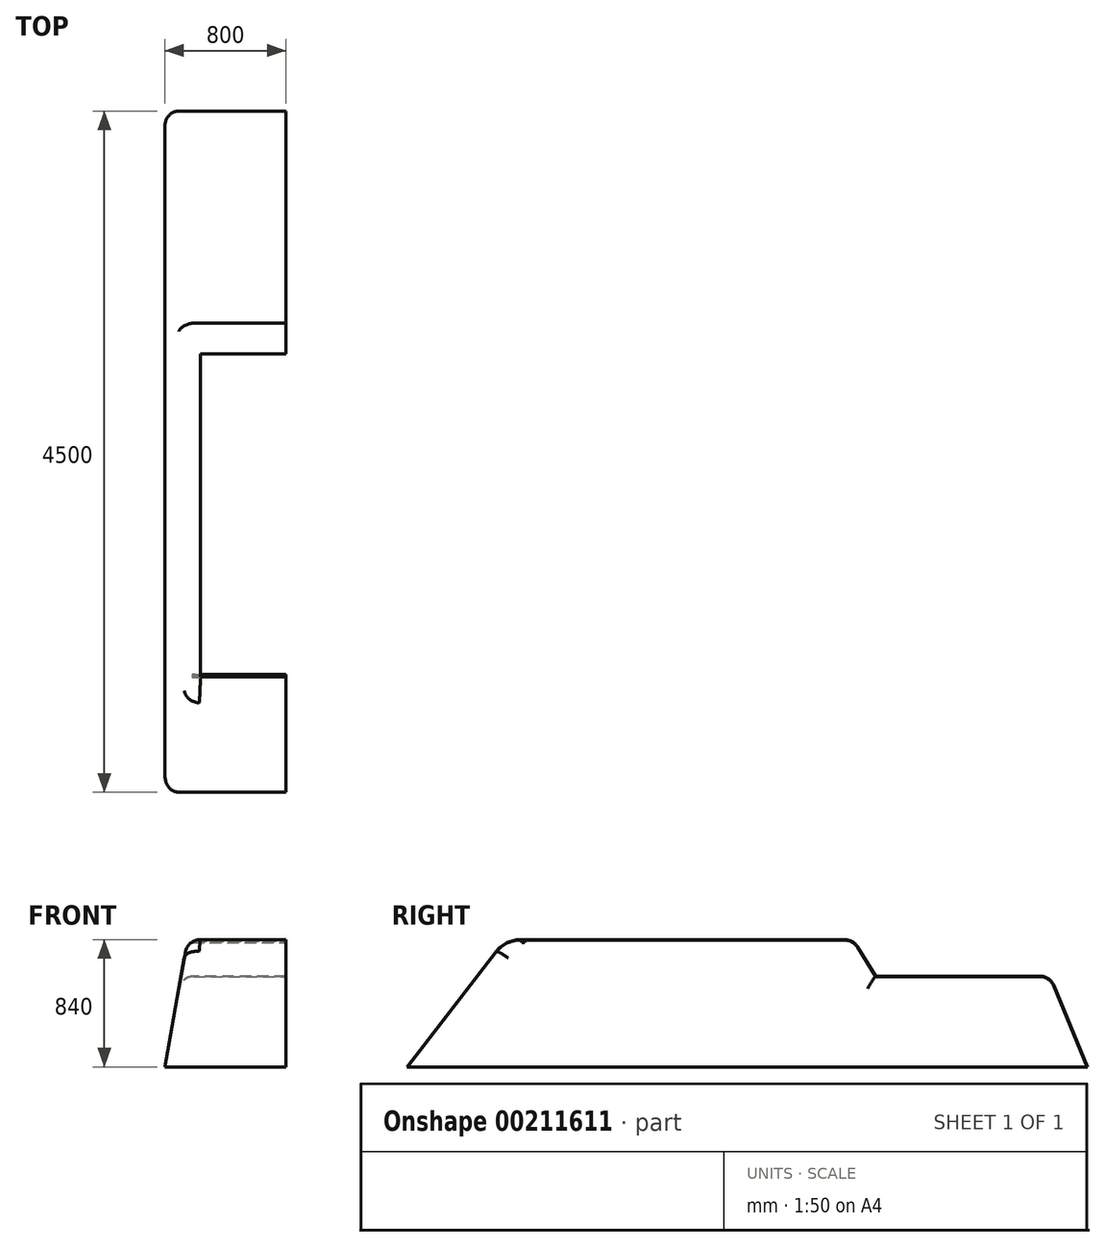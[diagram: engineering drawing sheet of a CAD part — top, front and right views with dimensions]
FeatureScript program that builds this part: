
annotation { "Feature Type Name" : "Feature", "Feature Type Description" : "" }
export const myFeature = defineFeature(function(context is Context, id is Id, definition is map)
    precondition{}
    {
        {
            var Q0;
            Q0=qCreatedBy(makeId("Right.planeOp"),FACE);
            var sketch = newSketch(context, id + "F0", { "sketchPlane" : qUnion([Q0])});
            skLineSegment(sketch, "E0", {"start": v(-1464.52, 0) * mm, "end": v(-874.57, 762.4) * mm});
            skLineSegment(sketch, "E1", {"start": v(-716.4, 840) * mm, "end": v(1430.05, 840) * mm});
            skLineSegment(sketch, "E2", {"start": v(1514.85, 793) * mm, "end": v(1635.48, 600) * mm});
            skLineSegment(sketch, "E3", {"start": v(1635.48, 600) * mm, "end": v(2718.81, 600) * mm});
            skLineSegment(sketch, "E4", {"start": v(2811.12, 538.46) * mm, "end": v(3035.48, 0) * mm});
            skLineSegment(sketch, "E5", {"start": v(3035.48, 0) * mm, "end": v(-1464.52, 0) * mm});
            skPoint(sketch, "E6.visualSharp", {"position": v(-814.52, 840) * mm});
            skArc(sketch, "E6.filletArc", {"start": v(-716.4, 840) * mm, "mid": v(-804.5, 819.55) * mm, "end": v(-874.57, 762.4) * mm});
            skPoint(sketch, "E7.visualSharp", {"position": v(1485.48, 840) * mm});
            skArc(sketch, "E7.filletArc", {"start": v(1514.85, 793) * mm, "mid": v(1478.53, 827.46) * mm, "end": v(1430.05, 840) * mm});
            skPoint(sketch, "E8.visualSharp", {"position": v(2785.48, 600) * mm});
            skArc(sketch, "E8.filletArc", {"start": v(2811.12, 538.46) * mm, "mid": v(2774.28, 583.2) * mm, "end": v(2718.81, 600) * mm});
            skSolve(sketch);
        }
        {
            var Q0;
            Q0=makeQuery(id+"F0.imprint","IMPRINT",FACE,{"disambiguationData":[TD([[makeQuery(id+"F0.imprint","IMPRINT",EDGE,{"derivedFrom":sQuery(id+"F0.wireOp",EDGE,"E0")}),-1.0]])]});
            var Q1;
            Q1=qSketchRegion(id+"FQhckZ4ycMq1syb_1",true);
            extrude(context, id + "F1", {"entities" : qUnion([Q0, Q1]), "depth" : 800 * mm});
        }
        {
            var Q0;
            Q0=qCreatedBy(makeId("Front.planeOp"),FACE);
            var sketch = newSketch(context, id + "F2", { "sketchPlane" : qUnion([Q0])});
            skLineSegment(sketch, "E9", {"start": v(0, 0) * mm, "end": v(0, 840) * mm});
            skLineSegment(sketch, "E10", {"start": v(0, 840) * mm, "end": v(150, 840) * mm});
            skLineSegment(sketch, "E11", {"start": v(150, 840) * mm, "end": v(0, 0) * mm});
            skSolve(sketch);
        }
        {
            var Q0;
            Q0=qSketchRegion(id+"F2",true);
            extrude(context, id + "F3", {"entities" : qUnion([Q0]), "operationType" : NewBodyOperationType.REMOVE, "oppositeDirection" : true, "depth" : 3490 * mm, "hasSecondDirection" : true, "secondDirectionOppositeDirection" : false, "secondDirectionDepth" : 1678 * mm});
        }
        {
            var Q0;
            Q0=makeQuery(id+"F3.boolean.opBoolean","INTERSECT",EDGE,{"derivedFrom":[makeQuery(id+"F1.opExtrude","SWEPT_FACE",FACE,{"disambiguationData":[OSD([sQuery(id+"F0.wireOp",EDGE,"E0")])]}),makeQuery(id+"F3.opExtrude","SWEPT_FACE",FACE,{"disambiguationData":[OSD([sQuery(id+"F2.wireOp",EDGE,"E11")])]})]});
            var Q1;
            Q1=makeQuery(id+"F3.boolean.opBoolean","COPY",EDGE,{"derivedFrom":makeQuery(id+"F3.opExtrude","SWEPT_EDGE",EDGE,{"disambiguationData":[OSD([sQuery(id+"F2.wireOp",EDGE,"E10"),sQuery(id+"F2.wireOp",EDGE,"E11")])]})});
            var Q2;
            Q2=makeQuery(id+"F3.boolean.opBoolean","INTERSECT",EDGE,{"derivedFrom":[makeQuery(id+"F1.opExtrude","SWEPT_FACE",FACE,{"disambiguationData":[OSD([sQuery(id+"F0.wireOp",EDGE,"E6.filletArc")])]}),makeQuery(id+"F3.opExtrude","SWEPT_FACE",FACE,{"disambiguationData":[OSD([sQuery(id+"F2.wireOp",EDGE,"E11")])]})]});
            var Q3;
            Q3=makeQuery(id+"F3.boolean.opBoolean","INTERSECT",EDGE,{"derivedFrom":[makeQuery(id+"F1.opExtrude","SWEPT_FACE",FACE,{"disambiguationData":[OSD([sQuery(id+"F0.wireOp",EDGE,"E2")])]}),makeQuery(id+"F3.opExtrude","SWEPT_FACE",FACE,{"disambiguationData":[OSD([sQuery(id+"F2.wireOp",EDGE,"E11")])]})]});
            var Q4;
            Q4=makeQuery(id+"F3.boolean.opBoolean","INTERSECT",EDGE,{"derivedFrom":[makeQuery(id+"F1.opExtrude","SWEPT_FACE",FACE,{"disambiguationData":[OSD([sQuery(id+"F0.wireOp",EDGE,"E7.filletArc")])]}),makeQuery(id+"F3.opExtrude","SWEPT_FACE",FACE,{"disambiguationData":[OSD([sQuery(id+"F2.wireOp",EDGE,"E11")])]})]});
            var Q5;
            Q5=makeQuery(id+"F3.boolean.opBoolean","INTERSECT",EDGE,{"derivedFrom":[makeQuery(id+"F1.opExtrude","SWEPT_FACE",FACE,{"disambiguationData":[OSD([sQuery(id+"F0.wireOp",EDGE,"E3")])]}),makeQuery(id+"F3.opExtrude","SWEPT_FACE",FACE,{"disambiguationData":[OSD([sQuery(id+"F2.wireOp",EDGE,"E11")])]})]});
            var Q6;
            Q6=makeQuery(id+"F3.boolean.opBoolean","INTERSECT",EDGE,{"derivedFrom":[makeQuery(id+"F1.opExtrude","SWEPT_FACE",FACE,{"disambiguationData":[OSD([sQuery(id+"F0.wireOp",EDGE,"E8.filletArc")])]}),makeQuery(id+"F3.opExtrude","SWEPT_FACE",FACE,{"disambiguationData":[OSD([sQuery(id+"F2.wireOp",EDGE,"E11")])]})]});
            var Q7;
            Q7=makeQuery(id+"F3.boolean.opBoolean","INTERSECT",EDGE,{"derivedFrom":[makeQuery(id+"F1.opExtrude","SWEPT_FACE",FACE,{"disambiguationData":[OSD([sQuery(id+"F0.wireOp",EDGE,"E4")])]}),makeQuery(id+"F3.opExtrude","SWEPT_FACE",FACE,{"disambiguationData":[OSD([sQuery(id+"F2.wireOp",EDGE,"E11")])]})]});
            fillet(context, id + "F4", {"entities" : qUnion([Q0, Q1, Q2, Q3, Q4, Q5, Q6, Q7]), "radius" : 100 * mm, "tangentPropagation" : true, "allowEdgeOverflow" : false});
        }
        {
            var Q0;
            Q0=makeQuery(id+"F1.opExtrude","SWEPT_FACE",FACE,{"disambiguationData":[OSD([sQuery(id+"F0.wireOp",EDGE,"E5")])]});
            var Q1;
            Q1=makeQuery(id+"F1.opExtrude","CAP_FACE",FACE,{"disambiguationData":[OSD([sQuery(id+"F0.wireOp",EDGE,"E0"),sQuery(id+"F0.wireOp",EDGE,"E1"),sQuery(id+"F0.wireOp",EDGE,"E2"),sQuery(id+"F0.wireOp",EDGE,"E3"),sQuery(id+"F0.wireOp",EDGE,"E4"),sQuery(id+"F0.wireOp",EDGE,"E5"),sQuery(id+"F0.wireOp",EDGE,"E6.filletArc"),sQuery(id+"F0.wireOp",EDGE,"E7.filletArc"),sQuery(id+"F0.wireOp",EDGE,"E8.filletArc")])],"isStart":false});
            shell(context, id + "F5", {"entities" : qUnion([Q0, Q1]), "thickness" : 3 * mm});
        }
        {
            var Q0;
            Q0=makeQuery(id+"F1.opExtrude","CAP_FACE",FACE,{"disambiguationData":[OSD([sQuery(id+"F0.wireOp",EDGE,"E0"),sQuery(id+"F0.wireOp",EDGE,"E1"),sQuery(id+"F0.wireOp",EDGE,"E2"),sQuery(id+"F0.wireOp",EDGE,"E3"),sQuery(id+"F0.wireOp",EDGE,"E4"),sQuery(id+"F0.wireOp",EDGE,"E5"),sQuery(id+"F0.wireOp",EDGE,"E6.filletArc"),sQuery(id+"F0.wireOp",EDGE,"E7.filletArc"),sQuery(id+"F0.wireOp",EDGE,"E8.filletArc")])],"isStart":false});
            var sketch = newSketch(context, id + "F6", { "sketchPlane" : qUnion([Q0])});
            skLineSegment(sketch, "E12", {"start": v(-703.4, 837) * mm, "end": v(-703.4, 825) * mm});
            skLineSegment(sketch, "E13", {"start": v(-703.4, 825) * mm, "end": v(-688.4, 825) * mm});
            skLineSegment(sketch, "E14", {"start": v(-688.4, 825) * mm, "end": v(-688.4, 831.31) * mm});
            skLineSegment(sketch, "E15", {"start": v(-688.4, 831.31) * mm, "end": v(-685.4, 831.31) * mm});
            skLineSegment(sketch, "E16", {"start": v(-685.4, 831.31) * mm, "end": v(-685.4, 822) * mm});
            skLineSegment(sketch, "E17", {"start": v(-685.4, 822) * mm, "end": v(-706.4, 822) * mm});
            skLineSegment(sketch, "E18", {"start": v(-706.4, 822) * mm, "end": v(-706.4, 837) * mm});
            skLineSegment(sketch, "E19", {"start": v(-706.4, 837) * mm, "end": v(-703.4, 837) * mm});
            skSolve(sketch);
        }
        {
            var Q0;
            Q0=makeQuery(id+"F6.imprint","IMPRINT",FACE,{"disambiguationData":[TD([[makeQuery(id+"F6.imprint","IMPRINT",EDGE,{"derivedFrom":sQuery(id+"F6.wireOp",EDGE,"E12")}),-1.0]])]});
            var Q1;
            Q1=makeQuery(id+"F5.opShell","OFFSET_FACE",FACE,{"disambiguationData":[OSD([sQuery(id+"F2.wireOp",EDGE,"E11")])]});
            var Q2;
            Q2=makeQuery(id+"F5.opShell","OFFSET_FACE",FACE,{"disambiguationData":[OSD([sQuery(id+"F2.wireOp",EDGE,"E10"),sQuery(id+"F2.wireOp",EDGE,"E11")])]});
            var Q3;
            Q3=sQuery(id+"F6.wireOp",VERTEX,"E12.start");
            extrude(context, id + "F7", {"entities" : qUnion([Q0, Q1]), "operationType" : NewBodyOperationType.ADD, "endBound" : BoundingType.UP_TO_NEXT, "oppositeDirection" : true, "endBoundEntityFace" : qUnion([Q2]), "endBoundEntityVertex" : qUnion([Q3]), "depth" : 25 * mm});
        }
        {
            var Q0;
            {var subQ1=sQuery(id+"F0.wireOp",EDGE,"E7.filletArc");var subQ2=sQuery(id+"F0.wireOp",EDGE,"E1");Q0=makeQuery(id+"F7.boolean.opBoolean","SPLIT",FACE,{"disambiguationData":[TD([makeQuery(id+"F5.opShell","OFFSET_FACE",FACE,{"disambiguationData":[OSD([subQ1])]})])],"derivedFrom":makeQuery(id+"F5.opShell","OFFSET_FACE",FACE,{"disambiguationData":[OSD([subQ2])]})});}
            extrude(context, id + "F8", {"entities" : qUnion([Q0]), "operationType" : NewBodyOperationType.REMOVE, "oppositeDirection" : true, "depth" : 25 * mm});
        }
    });
